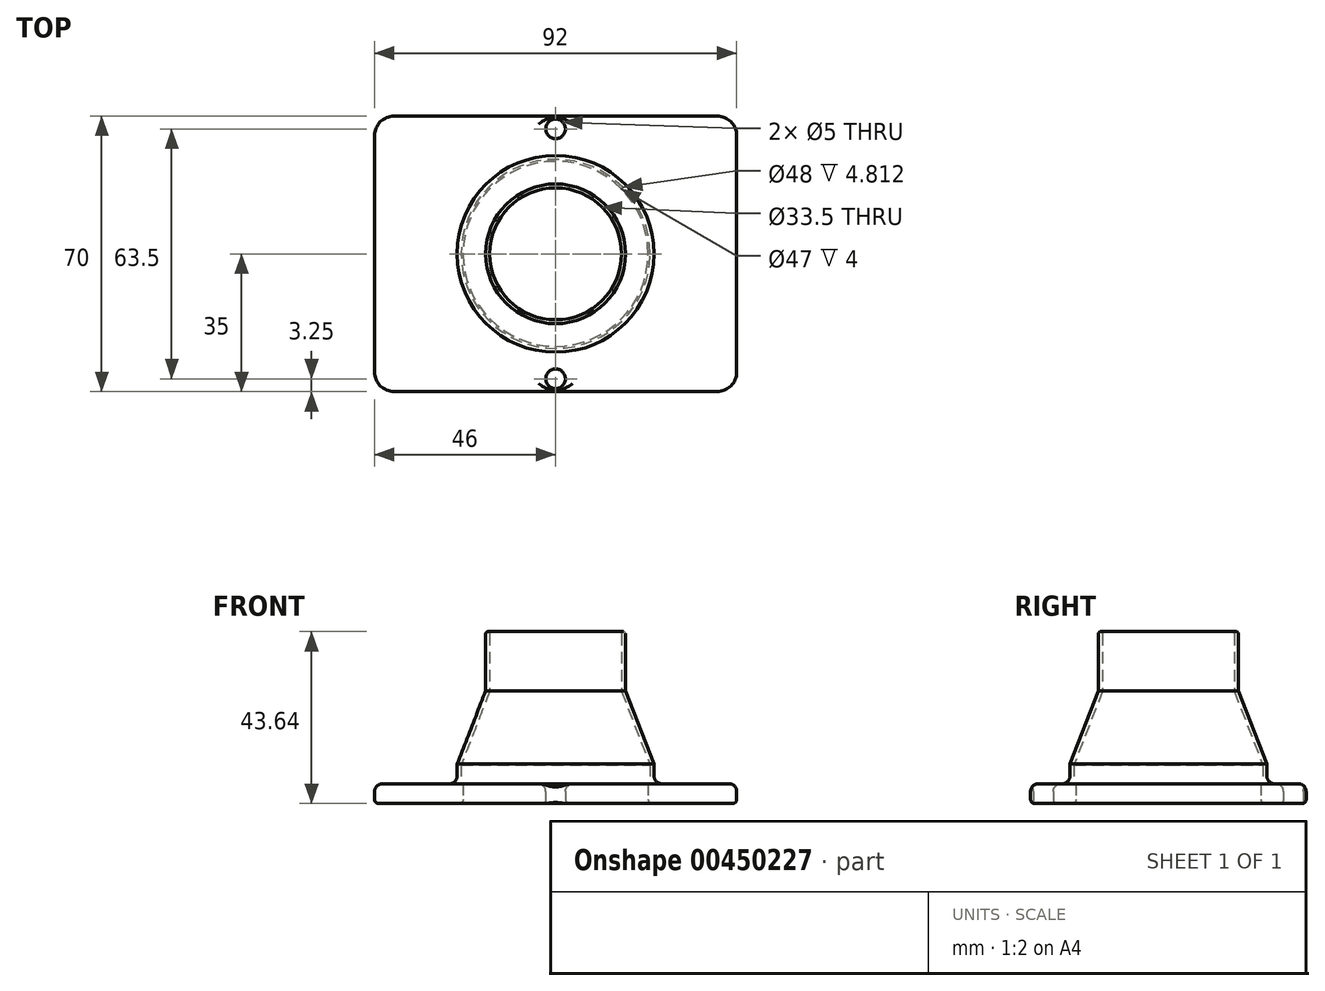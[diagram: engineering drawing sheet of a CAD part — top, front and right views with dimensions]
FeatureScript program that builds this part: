
annotation { "Feature Type Name" : "Feature", "Feature Type Description" : "" }
export const myFeature = defineFeature(function(context is Context, id is Id, definition is map)
    precondition{}
    {
        {
            var Q0;
            Q0=qCreatedBy(makeId("Front.planeOp"),FACE);
            var sketch = newSketch(context, id + "F0", { "sketchPlane" : qUnion([Q0])});
            skLineSegment(sketch, "E0", {"start": v(-25, 0) * mm, "end": v(-25, 10) * mm});
            skLineSegment(sketch, "E1", {"start": v(-25, 10) * mm, "end": v(-17.75, 28.64) * mm});
            skLineSegment(sketch, "E2", {"start": v(-17.75, 28.64) * mm, "end": v(-17.75, 43.64) * mm});
            skLineSegment(sketch, "E3.0", {"start": v(-16.75, 28.45) * mm, "end": v(-16.75, 43.64) * mm});
            skLineSegment(sketch, "E3.1", {"start": v(-24, 9.81) * mm, "end": v(-16.75, 28.45) * mm});
            skLineSegment(sketch, "E3.2", {"start": v(-24, 0) * mm, "end": v(-24, 9.81) * mm});
            skLineSegment(sketch, "E4", {"start": v(-25, 0) * mm, "end": v(-24, 0) * mm});
            skLineSegment(sketch, "E5", {"start": v(-17.75, 43.64) * mm, "end": v(-16.75, 43.64) * mm});
            skLineSegment(sketch, "E6", {"start": v(0, 0) * mm, "end": v(0, 46.9) * mm, "construction": true});
            skSolve(sketch);
        }
        {
            var Q0;
            Q0=makeQuery(id+"F0.imprint","IMPRINT",FACE,{"disambiguationData":[TD([[makeQuery(id+"F0.imprint","IMPRINT",EDGE,{"derivedFrom":sQuery(id+"F0.wireOp",EDGE,"E0")}),-1.0]])]});
            var Q1;
            Q1=sQuery(id+"F0.wireOp",EDGE,"E6");
            revolve(context, id + "F1", {"entities" : qUnion([Q0]), "axis" : qUnion([Q1]), "revolveType" : RevolveType.FULL});
        }
        {
            var Q0;
            Q0=makeQuery(id+"F1.opRevolve","SWEPT_FACE",FACE,{"disambiguationData":[OSD([sQuery(id+"F0.wireOp",EDGE,"E4")])]});
            cPlane(context, id + "F2", {"entities" : qUnion([Q0]), "cplaneType" : CPlaneType.OFFSET, "offset" : 0 * mm, "width" : 150 * mm, "height" : 150 * mm});
        }
        {
            var Q0;
            Q0=qCreatedBy(id+"F2.planeOp",FACE);
            var sketch = newSketch(context, id + "F3", { "sketchPlane" : qUnion([Q0])});
            skLineSegment(sketch, "E7.bottom", {"start": v(-46, 35) * mm, "end": v(46, 35) * mm});
            skLineSegment(sketch, "E7.top", {"start": v(-46, -35) * mm, "end": v(46, -35) * mm});
            skLineSegment(sketch, "E7.left", {"start": v(-46, 35) * mm, "end": v(-46, -35) * mm});
            skLineSegment(sketch, "E7.right", {"start": v(46, 35) * mm, "end": v(46, -35) * mm});
            skPoint(sketch, "E7.middle", {"position": v(0, 0) * mm});
            skLineSegment(sketch, "E8", {"start": v(0, 37.22) * mm, "end": v(0, -35) * mm, "construction": true});
            skCircle(sketch, "E9", {"center": v(0, 31.75) * mm, "radius": 2.5 * mm});
            skLineSegment(sketch, "E10", {"start": v(-42.64, 0) * mm, "end": v(31.16, 0) * mm, "construction": true});
            skCircle(sketch, "E11.MirrorC", {"center": v(0, -31.75) * mm, "radius": 2.5 * mm});
            skSolve(sketch);
        }
        {
            var Q0;
            Q0=makeQuery(id+"F3.imprint","IMPRINT",FACE,{"disambiguationData":[TD([[makeQuery(id+"F3.imprint","IMPRINT",EDGE,{"derivedFrom":sQuery(id+"F3.wireOp",EDGE,"E7.bottom")}),-1.0]])]});
            extrude(context, id + "F4", {"entities" : qUnion([Q0]), "operationType" : NewBodyOperationType.ADD, "oppositeDirection" : true, "depth" : 5 * mm});
        }
        {
            var Q0;
            Q0=makeQuery(id+"F4.boolean.opBoolean","MERGE",FACE,{"derivedFrom":[makeQuery(id+"F1.opRevolve","SWEPT_FACE",FACE,{"disambiguationData":[OSD([sQuery(id+"F0.wireOp",EDGE,"E4")])]}),makeQuery(id+"F4.opExtrude","CAP_FACE",FACE,{"disambiguationData":[OSD([sQuery(id+"F3.wireOp",EDGE,"E7.bottom"),sQuery(id+"F3.wireOp",EDGE,"E7.top"),sQuery(id+"F3.wireOp",EDGE,"E7.left"),sQuery(id+"F3.wireOp",EDGE,"E7.right"),sQuery(id+"F3.wireOp",EDGE,"E9"),sQuery(id+"F3.wireOp",EDGE,"E11.MirrorC")])],"isStart":true})]});
            var sketch = newSketch(context, id + "F5", { "sketchPlane" : qUnion([Q0])});
            skCircle(sketch, "E12", {"center": v(0, 0) * mm, "radius": 23.5 * mm});
            skSolve(sketch);
        }
        {
            var Q0;
            Q0=qSketchRegion(id+"F5",true);
            extrude(context, id + "F6", {"entities" : qUnion([Q0]), "operationType" : NewBodyOperationType.REMOVE, "endBound" : BoundingType.UP_TO_NEXT, "oppositeDirection" : true, "depth" : 25 * mm});
        }
        {
            var Q0;
            {var subQ0=sQuery(id+"F3.wireOp",EDGE,"E7.left");var subQ1=sQuery(id+"F3.wireOp",EDGE,"E7.top");var subQ2=sQuery(id+"F3.wireOp",EDGE,"E7.bottom");var subQ3=sQuery(id+"F3.wireOp",EDGE,"E9");var subQ4=sQuery(id+"F3.wireOp",EDGE,"E7.right");var subQ5=sQuery(id+"F3.wireOp",EDGE,"E11.MirrorC");Q0=makeQuery(id+"F4.boolean.opBoolean","SPLIT",FACE,{"disambiguationData":[TD([makeQuery(id+"F1.opRevolve","SWEPT_FACE",FACE,{"disambiguationData":[OSD([sQuery(id+"F0.wireOp",EDGE,"E0")])]})])],"derivedFrom":makeQuery(id+"F4.opExtrude","CAP_FACE",FACE,{"disambiguationData":[OSD([subQ2,subQ1,subQ0,subQ4,subQ3,subQ5])],"isStart":false})});}
            fillet(context, id + "F7", {"entities" : qUnion([Q0]), "radius" : 2 * mm, "tangentPropagation" : true, "allowEdgeOverflow" : false});
        }
        {
            var Q0;
            Q0=makeQuery(id+"F4.opExtrude","SWEPT_EDGE",EDGE,{"disambiguationData":[OSD([sQuery(id+"F3.wireOp",EDGE,"E7.bottom"),sQuery(id+"F3.wireOp",EDGE,"E7.right")])]});
            var Q1;
            Q1=makeQuery(id+"F4.opExtrude","SWEPT_EDGE",EDGE,{"disambiguationData":[OSD([sQuery(id+"F3.wireOp",EDGE,"E7.bottom"),sQuery(id+"F3.wireOp",EDGE,"E7.left")])]});
            var Q2;
            Q2=makeQuery(id+"F4.opExtrude","SWEPT_EDGE",EDGE,{"disambiguationData":[OSD([sQuery(id+"F3.wireOp",EDGE,"E7.top"),sQuery(id+"F3.wireOp",EDGE,"E7.left")])]});
            var Q3;
            Q3=makeQuery(id+"F4.opExtrude","SWEPT_EDGE",EDGE,{"disambiguationData":[OSD([sQuery(id+"F3.wireOp",EDGE,"E7.top"),sQuery(id+"F3.wireOp",EDGE,"E7.right")])]});
            fillet(context, id + "F8", {"entities" : qUnion([Q0, Q1, Q2, Q3]), "radius" : 5 * mm, "tangentPropagation" : true, "allowEdgeOverflow" : false});
        }
        {
            var Q0;
            Q0=makeQuery(id+"F1.opRevolve","SWEPT_FACE",FACE,{"disambiguationData":[OSD([sQuery(id+"F0.wireOp",EDGE,"E5")])]});
            fillet(context, id + "F9", {"entities" : qUnion([Q0]), "radius" : .5 * mm, "tangentPropagation" : true, "allowEdgeOverflow" : false});
        }
        {
            var Q0;
            Q0=makeQuery(id+"F4.boolean.opBoolean","MERGE",FACE,{"derivedFrom":[makeQuery(id+"F1.opRevolve","SWEPT_FACE",FACE,{"disambiguationData":[OSD([sQuery(id+"F0.wireOp",EDGE,"E4")])]}),makeQuery(id+"F4.opExtrude","CAP_FACE",FACE,{"disambiguationData":[OSD([sQuery(id+"F3.wireOp",EDGE,"E7.bottom"),sQuery(id+"F3.wireOp",EDGE,"E7.top"),sQuery(id+"F3.wireOp",EDGE,"E7.left"),sQuery(id+"F3.wireOp",EDGE,"E7.right"),sQuery(id+"F3.wireOp",EDGE,"E9"),sQuery(id+"F3.wireOp",EDGE,"E11.MirrorC")])],"isStart":true})]});
            fillet(context, id + "F10", {"entities" : qUnion([Q0]), "radius" : 1 * mm, "tangentPropagation" : true, "allowEdgeOverflow" : false});
        }
    });
